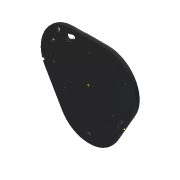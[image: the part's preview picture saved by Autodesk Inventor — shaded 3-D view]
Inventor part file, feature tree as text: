
AUTODESK INVENTOR PART (.ipt)
format: ipt  version: 2016 (Build 200138000, 138)  size: 397,312 bytes
history: native  units: mm
features: reference x45, sketch x18, extrude x15, thread x4, hole x3, pattern_circular x2
ambient origin geometry x8: Origin, YZ Plane, XZ Plane, XY Plane, X Axis, Y Axis, Z Axis, Center Point
bodies: Body1 (feature_tree)
feature tree (87):
  extrude  "Extrusion2"  Depth=10.0mm TaperAngle=0.0deg
  extrude  "Extrusion3"  Depth=10.0mm TaperAngle=0.0deg
  pattern_circular  "Circular Pattern1"  Count=3 Angle=360.0deg
  extrude  "Extrusion5"  Depth=10.0mm TaperAngle=0.0deg
  extrude  "Extrusion6"  Depth=3.3mm
  extrude  "Extrusion9"  Depth=3.3mm
  pattern_circular  "Circular Pattern2"  [2 undecoded]
  extrude  "Extrusion10"  Depth=10.0mm TaperAngle=0.0deg
  extrude  "Extrusion11"  Depth=10.0mm TaperAngle=0.0deg
  extrude  "Extrusion12"  Depth=10.0mm TaperAngle=0.0deg
  thread  "Thread1"  [1 undecoded]
  thread  "Thread2"  [1 undecoded]
  thread  "Thread3"  [1 undecoded]
  thread  "Thread4"  [1 undecoded]
  sketch  "Sketch15"  dims[d47=3.3mm d48=3.3mm]
  extrude  "Extrusion14"  Depth=10.0mm TaperAngle=0.0deg
  extrude  "Extrusion15"  Depth=5.0mm
  hole  "Hole1"  [1 undecoded]
  extrude  "Extrusion19"  Depth=3.5mm
  extrude  "Extrusion20"  Depth=16.7mm
  extrude  "Extrusion21"  Depth=10.0mm
  hole  "Hole2"  [1 undecoded]
  extrude  "Extrusion22"  Depth=10.0mm
  hole  "Hole3"  [1 undecoded]
  extrude  "Extrusion23"  Depth=10.0mm
  sketch  "Sketch28"  dims[d59=10.0mm d60=0.0mm d61=10.0mm d62=0.0mm d63=10.0mm d64=0.0mm d65=10.0mm d66=0.0mm d67=10.0mm d68=0.0mm d69=3.0mm d70=3.0mm d71=3.0mm d72=3.0mm d83=10.0mm d84=0.0mm d85=5.0mm d86=3.1mm d87=0.0mm d89=3.5mm d90=16.7mm d91=12.0mm d92=12.0mm d108=2.459mm d109=7.0mm d110=4.0mm d111=2.0mm d112=90.0deg d113=8.5mm d114=20.594885mm d118=18.0mm d119=89.0mm d120=53.0mm d121=12.0mm d122=25.0mm d123=70.0mm d124=10.0mm d125=0.0mm d126=10.0mm d127=20.0mm d128=20.0mm d129=0.0mm d130=8.5mm d131=110.0mm d132=30.0mm d134=360.0deg d136=10.0mm d137=0.0mm d148=3.242mm d149=7.0mm d150=4.0mm d151=2.0mm d152=90.0deg d153=8.5mm d154=20.594885mm d155=6.6mm d156=0.4mm d157=9.0mm d158=11.0mm d159=10.0mm d160=0.0mm d161=2.459mm d162=6.0mm d163=4.0mm d164=2.0mm d165=90.0deg d166=8.0mm d167=20.594885mm d168=10.0mm d169=0.0mm]
  sketch  "Sketch3"  dims[d9=10.0mm d10=0.0mm d11=10.0mm d12=0.0mm]
  reference  "Reference16"
  reference  "Reference17"
  reference  "Reference18"
  reference  "Reference19"
  reference  "Reference20"
  reference  "Reference21"
  reference  "Reference22"
  reference  "Reference23"
  reference  "Reference24"
  reference  "Reference25"
  reference  "Reference26"
  reference  "Reference27"
  reference  "Reference28"
  reference  "Reference29"
  reference  "Reference30"
  reference  "Reference31"
  sketch  "Sketch4"  dims[d13=30.0mm d14=360.0deg d23=10.0mm d24=0.0mm]
  reference  "Reference32"
  reference  "Reference33"
  reference  "Reference34"
  reference  "Reference35"
  reference  "Reference36"
  reference  "Reference37"
  reference  "Reference38"
  reference  "Reference39"
  reference  "Reference40"
  reference  "Reference41"
  sketch  "Sketch8"  dims[d25=0.5mm]
  reference  "Reference46"
  reference  "Reference47"
  reference  "Reference48"
  reference  "Reference49"
  sketch  "Sketch11"  dims[d26=0.5mm]
  sketch  "Sketch12"  dims[d29=6.3mm d30=0.0mm]
  reference  "Reference50"
  reference  "Reference51"
  sketch  "Sketch13"  dims[d38=10.0mm d39=0.0mm d40=30.0mm d41=360.0deg]
  sketch  "Sketch14"  dims[d43=3.0mm d44=0.0mm d45=10.0mm d46=0.0mm]
  reference  "Reference52"
  reference  "Reference53"
  reference  "Reference54"
  reference  "Reference55"
  sketch  "Sketch16"  dims[d49=3.3mm d50=3.3mm]
  reference  "Reference57"
  reference  "Reference58"
  reference  "Reference59"
  reference  "Reference60"
  sketch  "Sketch17"  dims[d51=5.8mm]
  sketch  "Sketch20"  dims[d52=5.8mm]
  reference  "Reference67"
  reference  "Reference68"
  reference  "Reference69"
  reference  "Reference70"
  reference  "Reference71"
  sketch  "Sketch22"  dims[d53=5.8mm]
  sketch  "Sketch23"  dims[d54=5.8mm]
  sketch  "Sketch24"  dims[d55=6.0mm]
  sketch  "Sketch25"  dims[d56=32.5mm]
  sketch  "Sketch26"  dims[d57=6.0mm]
  sketch  "Sketch27"  dims[d58=32.5mm]
note: 9 required parameter values undecoded (feature->parameter linkage not recoverable at this tier; creation-order binding heuristic only, values carry confidence <= 0.55)
